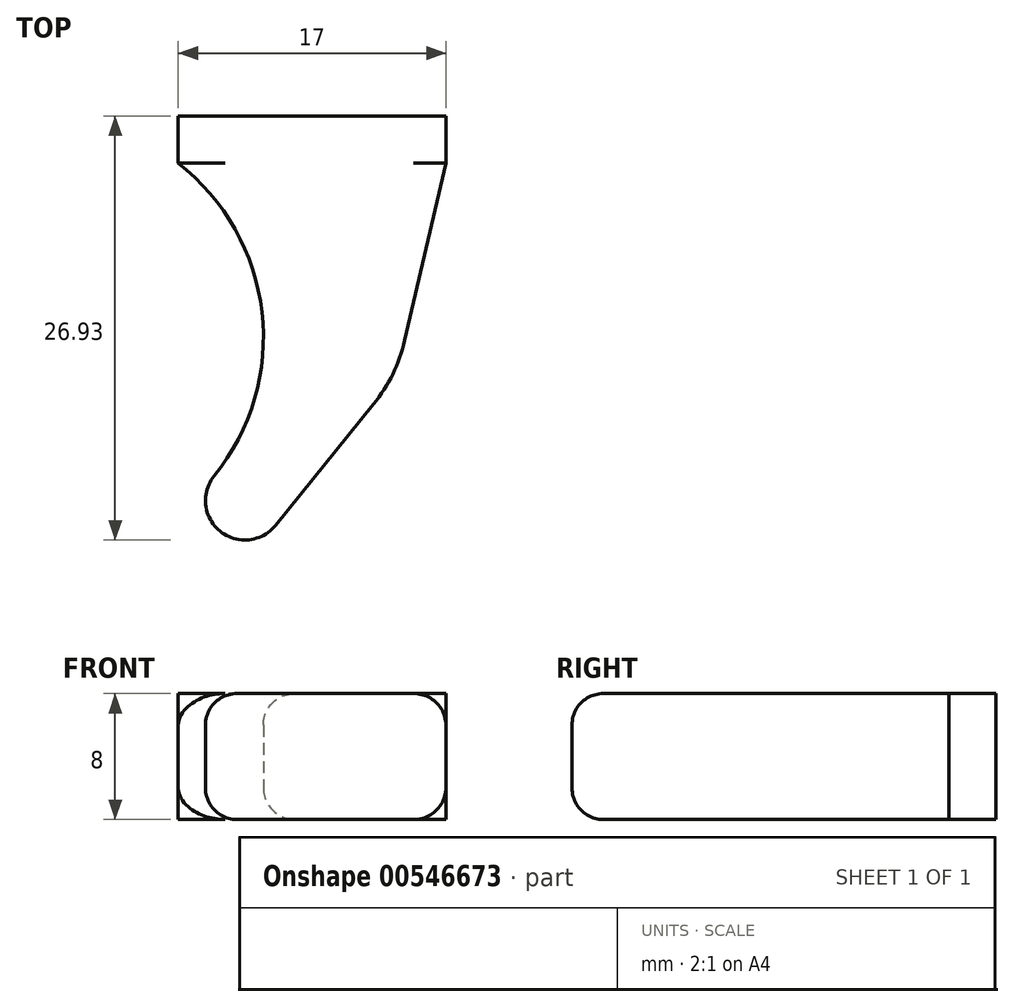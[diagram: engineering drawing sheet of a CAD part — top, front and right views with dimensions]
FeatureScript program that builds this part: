
annotation { "Feature Type Name" : "Feature", "Feature Type Description" : "" }
export const myFeature = defineFeature(function(context is Context, id is Id, definition is map)
    precondition{}
    {
        {
            var Q0;
            Q0=qCreatedBy(makeId("Top.planeOp"),FACE);
            var sketch = newSketch(context, id + "F0", { "sketchPlane" : qUnion([Q0])});
            skLineSegment(sketch, "E0", {"start": v(34.3, 0) * mm, "end": v(31.17, -13.5) * mm});
            skLineSegment(sketch, "E1", {"start": v(31.17, -13.5) * mm, "end": v(23.48, -23) * mm});
            skArc(sketch, "E2", {"start": v(19.6, -19.86) * mm, "mid": v(22.62, -9.45) * mm, "end": v(17.3, 0) * mm});
            skArc(sketch, "E3", {"start": v(19.6, -19.86) * mm, "mid": v(19.97, -23.37) * mm, "end": v(23.48, -23) * mm});
            skLineSegment(sketch, "E4", {"start": v(17.3, 0) * mm, "end": v(34.3, 0) * mm});
            skSolve(sketch);
        }
        {
            var Q0;
            Q0=qSketchRegion(id+"F0",true);
            extrude(context, id + "F1", {"entities" : qUnion([Q0]), "endBound" : BoundingType.SYMMETRIC, "depth" : 8 * mm});
        }
        {
            var Q0;
            Q0=makeQuery(id+"F1.opExtrude","SWEPT_EDGE",EDGE,{"disambiguationData":[OSD([sQuery(id+"F0.wireOp",EDGE,"E0"),sQuery(id+"F0.wireOp",EDGE,"E1")])]});
            fillet(context, id + "F2", {"entities" : qUnion([Q0]), "radius" : 10 * mm, "tangentPropagation" : true, "allowEdgeOverflow" : false});
        }
        {
            var Q0;
            Q0=makeQuery(id+"F1.opExtrude","CAP_EDGE",EDGE,{"disambiguationData":[OSD([sQuery(id+"F0.wireOp",EDGE,"E0")])],"isStart":false});
            var Q1;
            {var subQ0=sQuery(id+"F0.wireOp",EDGE,"E1");var subQ1=sQuery(id+"F0.wireOp",EDGE,"E0");Q1=makeQuery(id+"F2.opFillet","BLEND_EDGE",EDGE,{"blendedFrom":[makeQuery(id+"F1.opExtrude","SWEPT_EDGE",EDGE,{"disambiguationData":[OSD([subQ1,subQ0])]}),makeQuery(id+"F1.opExtrude","CAP_FACE",FACE,{"disambiguationData":[OSD([subQ1,subQ0,sQuery(id+"F0.wireOp",EDGE,"7X7qKE2I-nNr8-b8lX-uq4A-mIGdcvM5fNAC"),sQuery(id+"F0.wireOp",EDGE,"3254c177-f137-4f4f-9550-8d5c5fa8e2b2.0"),sQuery(id+"F0.wireOp",EDGE,"E2"),sQuery(id+"F0.wireOp",EDGE,"E3"),sQuery(id+"F0.wireOp",EDGE,"4dd9163c-d638-4e9a-84bb-52db589eff29.0")])],"isStart":false})],"blendedInto":[makeQuery(id+"F1.opExtrude","CAP_FACE",FACE,{"disambiguationData":[OSD([subQ1,subQ0,sQuery(id+"F0.wireOp",EDGE,"7X7qKE2I-nNr8-b8lX-uq4A-mIGdcvM5fNAC"),sQuery(id+"F0.wireOp",EDGE,"3254c177-f137-4f4f-9550-8d5c5fa8e2b2.0"),sQuery(id+"F0.wireOp",EDGE,"E2"),sQuery(id+"F0.wireOp",EDGE,"E3"),sQuery(id+"F0.wireOp",EDGE,"4dd9163c-d638-4e9a-84bb-52db589eff29.0")])],"isStart":false})]});}
            var Q2;
            Q2=makeQuery(id+"F1.opExtrude","CAP_EDGE",EDGE,{"disambiguationData":[OSD([sQuery(id+"F0.wireOp",EDGE,"E1")])],"isStart":false});
            var Q3;
            Q3=makeQuery(id+"F1.opExtrude","CAP_EDGE",EDGE,{"disambiguationData":[OSD([sQuery(id+"F0.wireOp",EDGE,"E3")])],"isStart":false});
            var Q4;
            Q4=makeQuery(id+"F1.opExtrude","CAP_EDGE",EDGE,{"disambiguationData":[OSD([sQuery(id+"F0.wireOp",EDGE,"E2")])],"isStart":false});
            var Q5;
            Q5=makeQuery(id+"F1.opExtrude","CAP_EDGE",EDGE,{"disambiguationData":[OSD([sQuery(id+"F0.wireOp",EDGE,"E2")])],"isStart":true});
            var Q6;
            Q6=makeQuery(id+"F1.opExtrude","CAP_EDGE",EDGE,{"disambiguationData":[OSD([sQuery(id+"F0.wireOp",EDGE,"E3")])],"isStart":true});
            var Q7;
            Q7=makeQuery(id+"F1.opExtrude","CAP_EDGE",EDGE,{"disambiguationData":[OSD([sQuery(id+"F0.wireOp",EDGE,"E1")])],"isStart":true});
            var Q8;
            {var subQ0=sQuery(id+"F0.wireOp",EDGE,"E1");var subQ1=sQuery(id+"F0.wireOp",EDGE,"E0");Q8=makeQuery(id+"F2.opFillet","BLEND_EDGE",EDGE,{"blendedFrom":[makeQuery(id+"F1.opExtrude","SWEPT_EDGE",EDGE,{"disambiguationData":[OSD([subQ1,subQ0])]}),makeQuery(id+"F1.opExtrude","CAP_FACE",FACE,{"disambiguationData":[OSD([subQ1,subQ0,sQuery(id+"F0.wireOp",EDGE,"7X7qKE2I-nNr8-b8lX-uq4A-mIGdcvM5fNAC"),sQuery(id+"F0.wireOp",EDGE,"3254c177-f137-4f4f-9550-8d5c5fa8e2b2.0"),sQuery(id+"F0.wireOp",EDGE,"E2"),sQuery(id+"F0.wireOp",EDGE,"E3"),sQuery(id+"F0.wireOp",EDGE,"4dd9163c-d638-4e9a-84bb-52db589eff29.0")])],"isStart":true})],"blendedInto":[makeQuery(id+"F1.opExtrude","CAP_FACE",FACE,{"disambiguationData":[OSD([subQ1,subQ0,sQuery(id+"F0.wireOp",EDGE,"7X7qKE2I-nNr8-b8lX-uq4A-mIGdcvM5fNAC"),sQuery(id+"F0.wireOp",EDGE,"3254c177-f137-4f4f-9550-8d5c5fa8e2b2.0"),sQuery(id+"F0.wireOp",EDGE,"E2"),sQuery(id+"F0.wireOp",EDGE,"E3"),sQuery(id+"F0.wireOp",EDGE,"4dd9163c-d638-4e9a-84bb-52db589eff29.0")])],"isStart":true})]});}
            var Q9;
            Q9=makeQuery(id+"F1.opExtrude","CAP_EDGE",EDGE,{"disambiguationData":[OSD([sQuery(id+"F0.wireOp",EDGE,"E0")])],"isStart":true});
            fillet(context, id + "F3", {"entities" : qUnion([Q0, Q1, Q2, Q3, Q4, Q5, Q6, Q7, Q8, Q9]), "radius" : 2 * mm, "tangentPropagation" : true, "allowEdgeOverflow" : false});
        }
        {
            var Q0;
            Q0=makeQuery(id+"F1.opExtrude","SWEPT_FACE",FACE,{"disambiguationData":[OSD([sQuery(id+"F0.wireOp",EDGE,"E4")])]});
            var sketch = newSketch(context, id + "F4", { "sketchPlane" : qUnion([Q0])});
            skLineSegment(sketch, "E5", {"start": v(-34.3, -4) * mm, "end": v(-34.3, 4) * mm});
            skLineSegment(sketch, "E6", {"start": v(-34.3, 4) * mm, "end": v(-17.3, 4) * mm});
            skLineSegment(sketch, "E7.MirrorCS", {"start": v(-34.3, -4) * mm, "end": v(-17.3, -4) * mm});
            skLineSegment(sketch, "E8", {"start": v(-17.3, -4) * mm, "end": v(-17.3, 4) * mm});
            skPoint(sketch, "E9.orphan", {"position": v(-20.28, -4) * mm});
            skSolve(sketch);
        }
        {
            var Q0;
            Q0=qSketchRegion(id+"F4",true);
            extrude(context, id + "F5", {"entities" : qUnion([Q0]), "operationType" : NewBodyOperationType.ADD, "depth" : 3 * mm});
        }
    });
